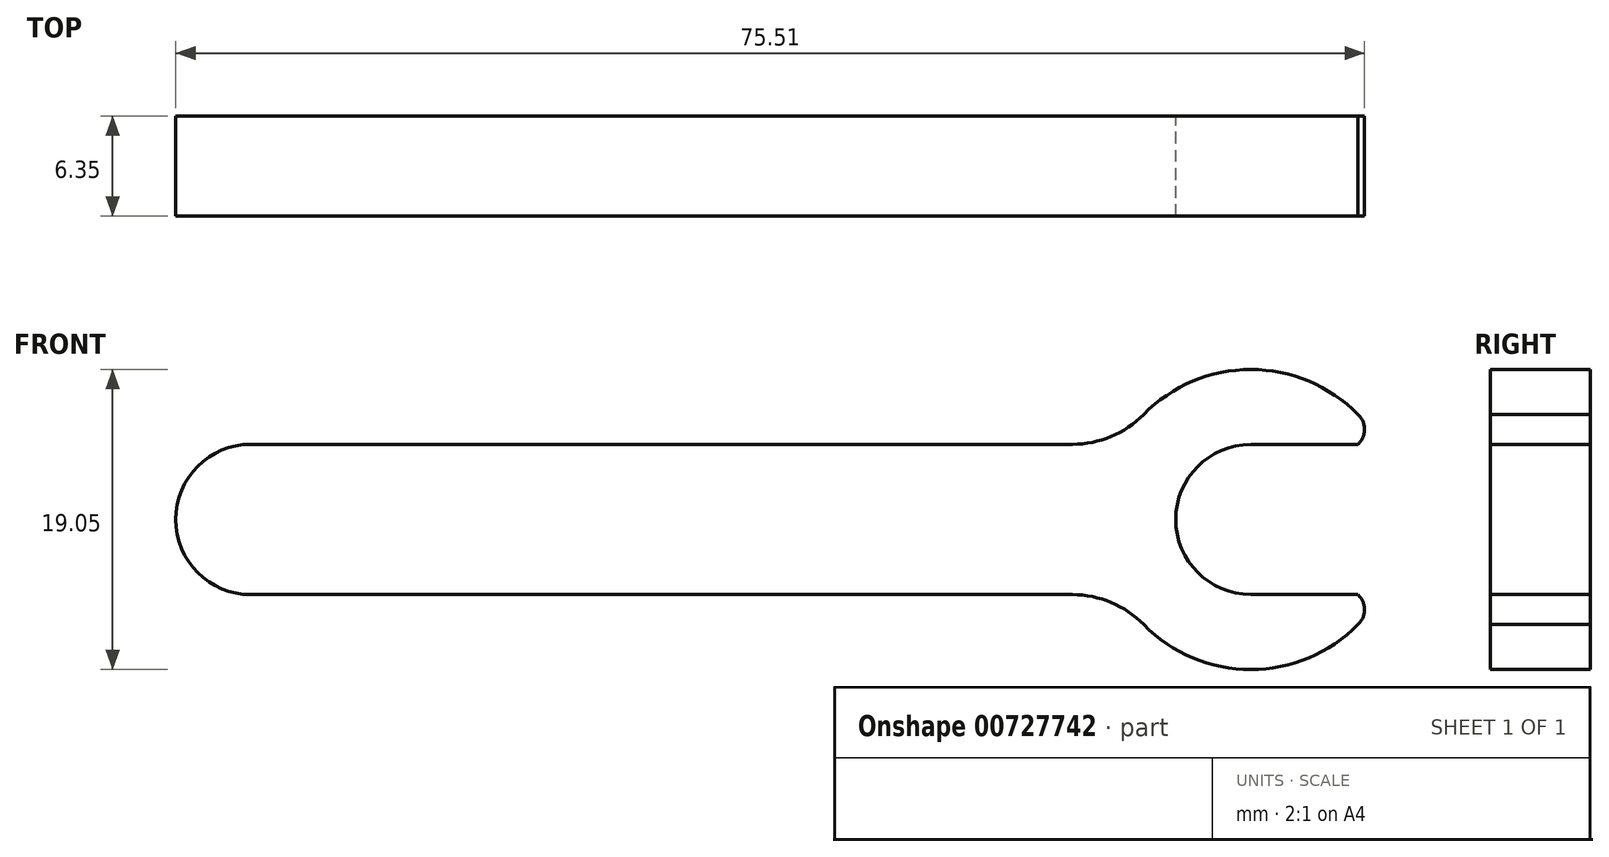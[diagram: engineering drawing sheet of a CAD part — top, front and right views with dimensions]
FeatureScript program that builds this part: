
annotation { "Feature Type Name" : "Feature", "Feature Type Description" : "" }
export const myFeature = defineFeature(function(context is Context, id is Id, definition is map)
    precondition{}
    {
        {
            var Q0;
            Q0=qCreatedBy(makeId("Front.planeOp"),FACE);
            var sketch = newSketch(context, id + "F0", { "sketchPlane" : qUnion([Q0])});
            skArc(sketch, "E0", {"start": v(0, 0) * mm, "mid": v(-4.78, -4.78) * mm, "end": v(0, -9.55) * mm});
            skLineSegment(sketch, "E1", {"start": v(0, 0) * mm, "end": v(52.18, 0) * mm});
            skLineSegment(sketch, "E2", {"start": v(0, -9.55) * mm, "end": v(52.18, -9.55) * mm});
            skArc(sketch, "E3", {"start": v(52.18, 0) * mm, "mid": v(54.63, 0.5) * mm, "end": v(56.7, 1.9) * mm});
            skArc(sketch, "E4", {"start": v(56.7, -11.45) * mm, "mid": v(54.63, -10.04) * mm, "end": v(52.18, -9.55) * mm});
            skArc(sketch, "E5", {"start": v(70.3, 1.9) * mm, "mid": v(63.5, 4.75) * mm, "end": v(56.7, 1.9) * mm});
            skLineSegment(sketch, "E6", {"start": v(0, -4.78) * mm, "end": v(83.46, -4.78) * mm, "construction": true});
            skLineSegment(sketch, "E7", {"start": v(0, 5.33) * mm, "end": v(0, -13.79) * mm, "construction": true});
            skArc(sketch, "E8", {"start": v(56.7, -11.45) * mm, "mid": v(63.5, -14.3) * mm, "end": v(70.3, -11.45) * mm});
            skLineSegment(sketch, "E9", {"start": v(63.5, -4.78) * mm, "end": v(63.5, -25.89) * mm, "construction": true});
            skLineSegment(sketch, "E10", {"start": v(56.7, 5.7) * mm, "end": v(56.7, -23.6) * mm, "construction": true});
            skArc(sketch, "E11", {"start": v(70.3, -11.45) * mm, "mid": v(70.73, -10.5) * mm, "end": v(70.3, -9.54) * mm});
            skArc(sketch, "E12", {"start": v(70.3, -0.01) * mm, "mid": v(70.73, 0.94) * mm, "end": v(70.3, 1.9) * mm});
            skLineSegment(sketch, "E13", {"start": v(70.3, -0.01) * mm, "end": v(63.5, -0.01) * mm});
            skLineSegment(sketch, "E14", {"start": v(70.3, -9.54) * mm, "end": v(63.5, -9.54) * mm});
            skArc(sketch, "E15", {"start": v(63.5, -0.01) * mm, "mid": v(58.74, -4.78) * mm, "end": v(63.5, -9.54) * mm});
            skLineSegment(sketch, "E16", {"start": v(69.46, -14.33) * mm, "end": v(69.46, 8.06) * mm, "construction": true});
            skSolve(sketch);
        }
        {
            var Q0;
            Q0 = qSketchRegion(id + "F0", true);
            extrude(context, id + "F1", {"entities" : qUnion([Q0]), "depth" : 6.35 * mm, "offsetDistance" : 25.4 * mm});
        }
    });
